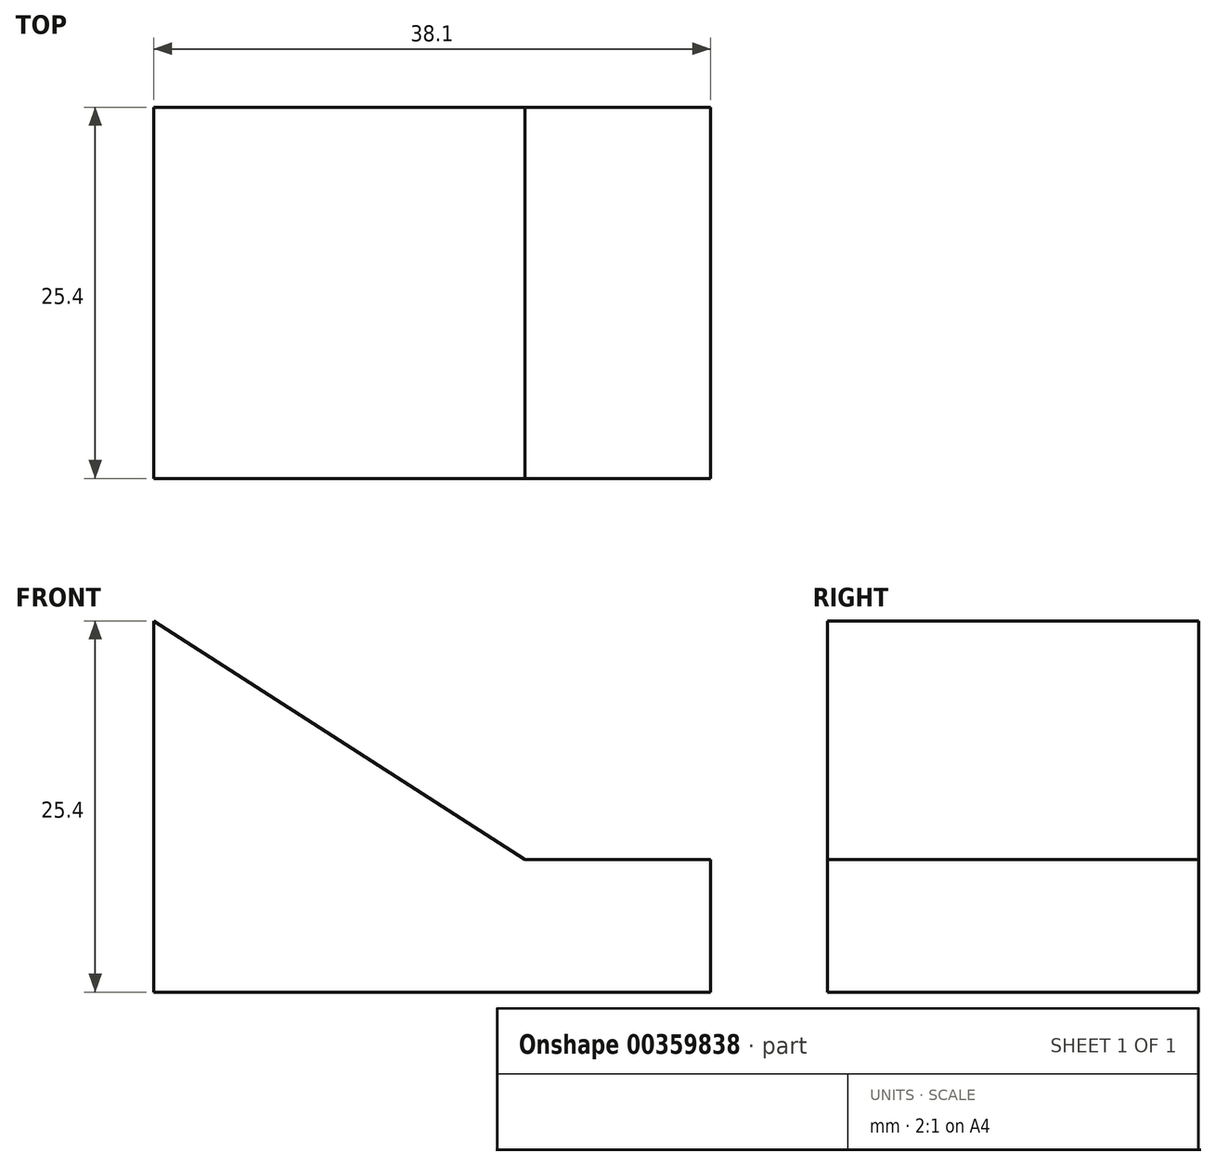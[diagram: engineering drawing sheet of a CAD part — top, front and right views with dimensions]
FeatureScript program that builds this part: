
annotation { "Feature Type Name" : "Feature", "Feature Type Description" : "" }
export const myFeature = defineFeature(function(context is Context, id is Id, definition is map)
    precondition{}
    {
        {
            var Q0;
            Q0=qCreatedBy(makeId("Front.planeOp"),FACE);
            var sketch = newSketch(context, id + "F0", { "sketchPlane" : qUnion([Q0])});
            skLineSegment(sketch, "E0", {"start": v(0, 0) * mm, "end": v(0, 25.4) * mm});
            skLineSegment(sketch, "E1", {"start": v(0, 25.4) * mm, "end": v(38.1, 25.4) * mm});
            skLineSegment(sketch, "E2", {"start": v(38.1, 25.4) * mm, "end": v(38.1, 0) * mm});
            skLineSegment(sketch, "E3", {"start": v(38.1, 0) * mm, "end": v(0, 0) * mm});
            skSolve(sketch);
        }
        {
            var Q0;
            Q0 = qSketchRegion(id + "F0", true);
            extrude(context, id + "F1", {"entities" : qUnion([Q0]), "depth" : 25.4 * mm});
        }
        {
            var Q0;
            Q0=makeQuery(id+"F1.opExtrude","CAP_FACE",FACE,{"disambiguationData":[OSD([sQuery(id+"F0.wireOp",EDGE,"E0"),sQuery(id+"F0.wireOp",EDGE,"E1"),sQuery(id+"F0.wireOp",EDGE,"E2"),sQuery(id+"F0.wireOp",EDGE,"E3")])],"isStart":false});
            var sketch = newSketch(context, id + "F2", { "sketchPlane" : qUnion([Q0])});
            skLineSegment(sketch, "E4", {"start": v(0, 25.4) * mm, "end": v(25.4, 9.08) * mm});
            skLineSegment(sketch, "E5", {"start": v(25.4, 9.08) * mm, "end": v(38.1, 9.08) * mm});
            skSolve(sketch);
        }
        {
            var Q0;
            Q0=makeQuery(id+"F2.imprint","IMPRINT",FACE,{"disambiguationData":[TD([[makeQuery(id+"F2.imprint","IMPRINT",EDGE,{"derivedFrom":sQuery(id+"F2.wireOp",EDGE,"E4")}),1.0]])]});
            extrude(context, id + "F3", {"entities" : qUnion([Q0]), "operationType" : NewBodyOperationType.REMOVE, "oppositeDirection" : true, "depth" : 25.4 * mm});
        }
    });
